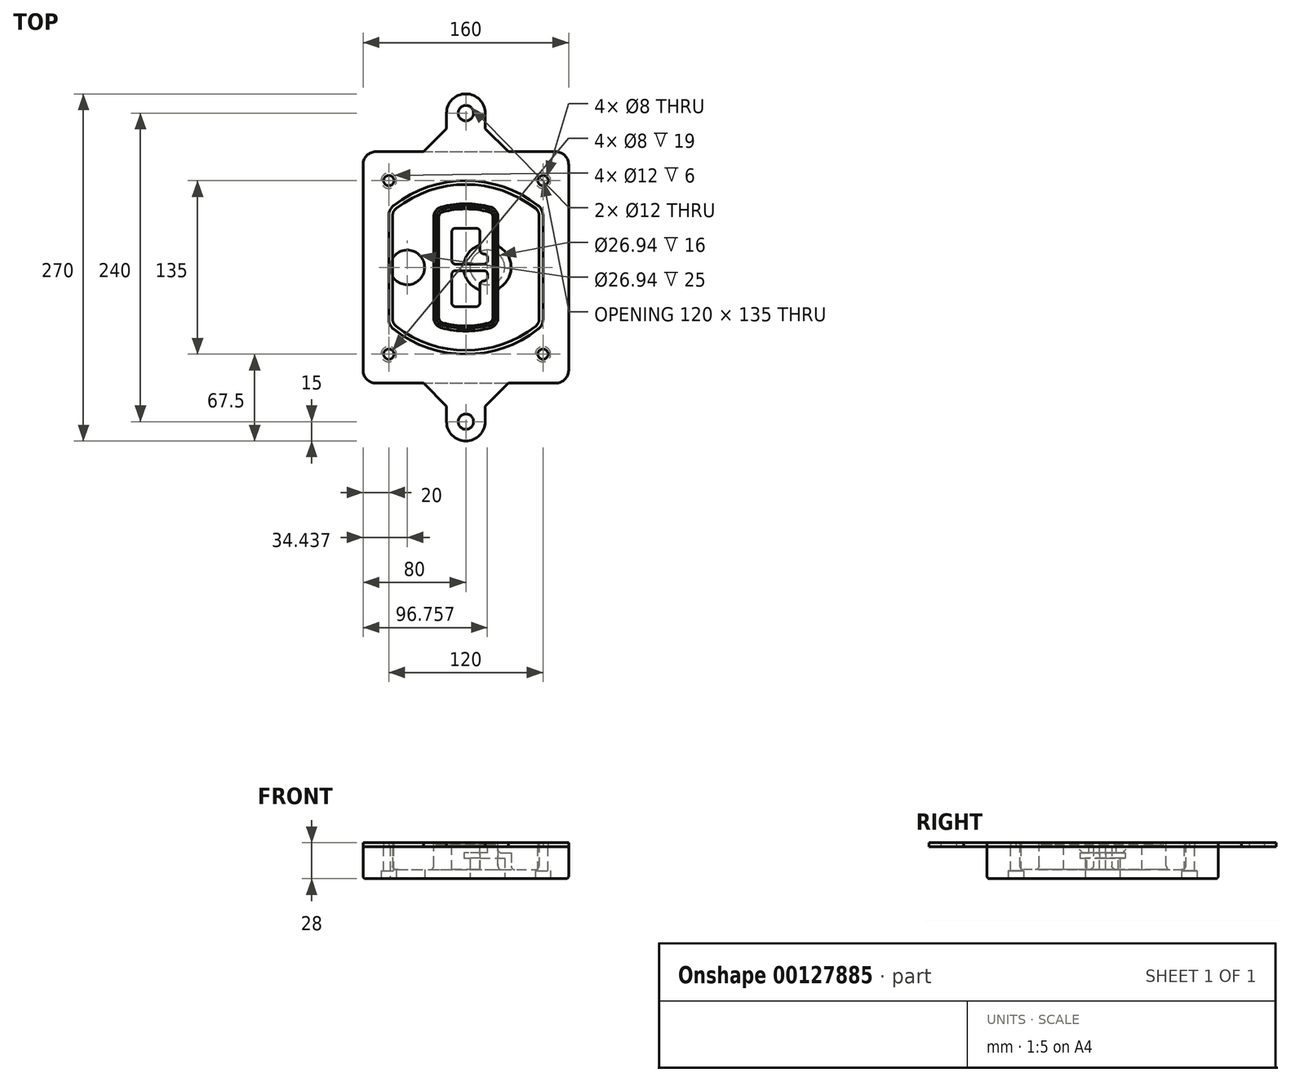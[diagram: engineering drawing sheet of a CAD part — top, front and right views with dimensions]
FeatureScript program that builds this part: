
annotation { "Feature Type Name" : "Feature", "Feature Type Description" : "" }
export const myFeature = defineFeature(function(context is Context, id is Id, definition is map)
    precondition{}
    {
        {
            var Q0;
            Q0=qCreatedBy(makeId("Top.planeOp"),FACE);
            var sketch = newSketch(context, id + "F0", { "sketchPlane" : qUnion([Q0])});
            skPoint(sketch, "E0.rect.middle", {"position": v(0, 0) * mm});
            skLineSegment(sketch, "E1.bottom", {"start": v(-70, -90) * mm, "end": v(70, -90) * mm});
            skLineSegment(sketch, "E1.top", {"start": v(-70, 90) * mm, "end": v(70, 90) * mm});
            skLineSegment(sketch, "E1.left", {"start": v(-80, -80) * mm, "end": v(-80, 80) * mm});
            skLineSegment(sketch, "E1.right", {"start": v(80, -80) * mm, "end": v(80, 80) * mm});
            skLineSegment(sketch, "E2", {"start": v(-80, 90) * mm, "end": v(80, -90) * mm, "construction": true});
            skLineSegment(sketch, "E3", {"start": v(80, 90) * mm, "end": v(-80, -90) * mm, "construction": true});
            skCircle(sketch, "E4", {"center": v(-60, 67.5) * mm, "radius": 4 * mm});
            skCircle(sketch, "E5", {"center": v(60, 67.5) * mm, "radius": 4 * mm});
            skCircle(sketch, "E6", {"center": v(60, -67.5) * mm, "radius": 4 * mm});
            skCircle(sketch, "E7", {"center": v(-60, -67.5) * mm, "radius": 4 * mm});
            skLineSegment(sketch, "E8", {"start": v(-60, 67.5) * mm, "end": v(60, 67.5) * mm, "construction": true});
            skLineSegment(sketch, "E9", {"start": v(60, 67.5) * mm, "end": v(60, -67.5) * mm, "construction": true});
            skLineSegment(sketch, "E10", {"start": v(60, -67.5) * mm, "end": v(-60, -67.5) * mm, "construction": true});
            skLineSegment(sketch, "E11", {"start": v(-60, -67.5) * mm, "end": v(-60, 67.5) * mm, "construction": true});
            skLineSegment(sketch, "E12", {"start": v(-60, 40.3) * mm, "end": v(-60, -40.3) * mm});
            skLineSegment(sketch, "E13", {"start": v(60, 40.3) * mm, "end": v(60, -40.3) * mm});
            skArc(sketch, "E14", {"start": v(56.15, 48.18) * mm, "mid": v(0, 67.5) * mm, "end": v(-56.15, 48.18) * mm});
            skArc(sketch, "E15", {"start": v(-56.15, -48.18) * mm, "mid": v(0, -67.5) * mm, "end": v(56.15, -48.18) * mm});
            skLineSegment(sketch, "E16", {"start": v(-60, 0) * mm, "end": v(60, 0) * mm, "construction": true});
            skPoint(sketch, "E17.visualSharp", {"position": v(-60, -45) * mm});
            skArc(sketch, "E17.filletArc", {"start": v(-60, -40.3) * mm, "mid": v(-58.99, -44.68) * mm, "end": v(-56.15, -48.18) * mm});
            skPoint(sketch, "E18.visualSharp", {"position": v(-60, 45) * mm});
            skArc(sketch, "E18.filletArc", {"start": v(-56.15, 48.18) * mm, "mid": v(-58.99, 44.68) * mm, "end": v(-60, 40.3) * mm});
            skPoint(sketch, "E19.visualSharp", {"position": v(60, 45) * mm});
            skArc(sketch, "E19.filletArc", {"start": v(60, 40.3) * mm, "mid": v(58.99, 44.68) * mm, "end": v(56.15, 48.18) * mm});
            skPoint(sketch, "E20.visualSharp", {"position": v(60, -45) * mm});
            skArc(sketch, "E20.filletArc", {"start": v(56.15, -48.18) * mm, "mid": v(58.99, -44.68) * mm, "end": v(60, -40.3) * mm});
            skPoint(sketch, "E21.visualSharp", {"position": v(-80, 90) * mm});
            skArc(sketch, "E21.filletArc", {"start": v(-70, 90) * mm, "mid": v(-77.07, 87.07) * mm, "end": v(-80, 80) * mm});
            skPoint(sketch, "E22.visualSharp", {"position": v(80, 90) * mm});
            skArc(sketch, "E22.filletArc", {"start": v(80, 80) * mm, "mid": v(77.07, 87.07) * mm, "end": v(70, 90) * mm});
            skPoint(sketch, "E23.visualSharp", {"position": v(80, -90) * mm});
            skArc(sketch, "E23.filletArc", {"start": v(70, -90) * mm, "mid": v(77.07, -87.07) * mm, "end": v(80, -80) * mm});
            skPoint(sketch, "E24.visualSharp", {"position": v(-80, -90) * mm});
            skArc(sketch, "E24.filletArc", {"start": v(-80, -80) * mm, "mid": v(-77.07, -87.07) * mm, "end": v(-70, -90) * mm});
            skArc(sketch, "E25.0", {"start": v(57, 40.3) * mm, "mid": v(56.3, 43.36) * mm, "end": v(54.3, 45.81) * mm});
            skLineSegment(sketch, "E25.1", {"start": v(57, 40.3) * mm, "end": v(57, -40.3) * mm});
            skArc(sketch, "E25.2", {"start": v(54.3, -45.81) * mm, "mid": v(56.3, -43.36) * mm, "end": v(57, -40.3) * mm});
            skArc(sketch, "E25.3", {"start": v(-54.3, -45.81) * mm, "mid": v(0, -64.5) * mm, "end": v(54.3, -45.81) * mm});
            skArc(sketch, "E25.4", {"start": v(-57, -40.3) * mm, "mid": v(-56.3, -43.36) * mm, "end": v(-54.3, -45.81) * mm});
            skArc(sketch, "E25.5", {"start": v(54.3, 45.81) * mm, "mid": v(0, 64.5) * mm, "end": v(-54.3, 45.81) * mm});
            skLineSegment(sketch, "E25.6", {"start": v(-57, 40.3) * mm, "end": v(-57, -40.3) * mm});
            skArc(sketch, "E25.7", {"start": v(-54.3, 45.81) * mm, "mid": v(-56.3, 43.36) * mm, "end": v(-57, 40.3) * mm});
            skArc(sketch, "E26.0", {"start": v(-58.62, 51.33) * mm, "mid": v(-62.58, 46.43) * mm, "end": v(-64, 40.3) * mm});
            skArc(sketch, "E26.1", {"start": v(58.62, 51.33) * mm, "mid": v(0, 71.5) * mm, "end": v(-58.62, 51.33) * mm});
            skArc(sketch, "E26.2", {"start": v(64, 40.3) * mm, "mid": v(62.58, 46.43) * mm, "end": v(58.62, 51.33) * mm});
            skLineSegment(sketch, "E26.3", {"start": v(64, 40.3) * mm, "end": v(64, -40.3) * mm});
            skArc(sketch, "E26.4", {"start": v(58.62, -51.33) * mm, "mid": v(62.58, -46.43) * mm, "end": v(64, -40.3) * mm});
            skLineSegment(sketch, "E26.5", {"start": v(-64, 40.3) * mm, "end": v(-64, -40.3) * mm});
            skArc(sketch, "E26.6", {"start": v(-58.62, -51.33) * mm, "mid": v(0, -71.5) * mm, "end": v(58.62, -51.33) * mm});
            skArc(sketch, "E26.7", {"start": v(-64, -40.3) * mm, "mid": v(-62.58, -46.43) * mm, "end": v(-58.62, -51.33) * mm});
            skSolve(sketch);
        }
        {
            var Q0;
            Q0=makeQuery(id+"F0.imprint","IMPRINT",FACE,{"disambiguationData":[TD([[makeQuery(id+"F0.imprint","IMPRINT",EDGE,{"derivedFrom":sQuery(id+"F0.wireOp",EDGE,"E1.bottom")}),1.0]])]});
            var Q1;
            Q1=makeQuery(id+"F0.imprint","IMPRINT",FACE,{"disambiguationData":[TD([[makeQuery(id+"F0.imprint","IMPRINT",EDGE,{"derivedFrom":sQuery(id+"F0.wireOp",EDGE,"E12")}),1.0]])]});
            var Q2;
            Q2=makeQuery(id+"F0.imprint","IMPRINT",FACE,{"disambiguationData":[TD([[makeQuery(id+"F0.imprint","IMPRINT",EDGE,{"derivedFrom":sQuery(id+"F0.wireOp",EDGE,"E25.0")}),1.0]])]});
            var Q3;
            Q3=makeQuery(id+"F0.imprint","IMPRINT",FACE,{"disambiguationData":[TD([[makeQuery(id+"F0.imprint","IMPRINT",EDGE,{"derivedFrom":sQuery(id+"F0.wireOp",EDGE,"E12")}),-1.0]])]});
            extrude(context, id + "F1", {"entities" : qUnion([Q0, Q1, Q2, Q3]), "oppositeDirection" : true, "depth" : 25 * mm});
        }
        {
            var Q0;
            Q0=makeQuery(id+"F0.imprint","IMPRINT",FACE,{"disambiguationData":[TD([[makeQuery(id+"F0.imprint","IMPRINT",EDGE,{"derivedFrom":sQuery(id+"F0.wireOp",EDGE,"E12")}),1.0]])]});
            extrude(context, id + "F2", {"entities" : qUnion([Q0]), "operationType" : NewBodyOperationType.ADD, "depth" : 3 * mm});
        }
        {
            var Q0;
            Q0=makeQuery(id+"F0.imprint","IMPRINT",FACE,{"disambiguationData":[TD([[makeQuery(id+"F0.imprint","IMPRINT",EDGE,{"derivedFrom":sQuery(id+"F0.wireOp",EDGE,"E25.0")}),1.0]])]});
            extrude(context, id + "F3", {"entities" : qUnion([Q0]), "operationType" : NewBodyOperationType.REMOVE, "oppositeDirection" : true, "depth" : 18 * mm});
        }
        {
            var Q0;
            Q0=makeQuery(id+"F2.opExtrude","CAP_FACE",FACE,{"disambiguationData":[OSD([sQuery(id+"F0.wireOp",EDGE,"E12"),sQuery(id+"F0.wireOp",EDGE,"E13"),sQuery(id+"F0.wireOp",EDGE,"E14"),sQuery(id+"F0.wireOp",EDGE,"E15"),sQuery(id+"F0.wireOp",EDGE,"E17.filletArc"),sQuery(id+"F0.wireOp",EDGE,"E18.filletArc"),sQuery(id+"F0.wireOp",EDGE,"E19.filletArc"),sQuery(id+"F0.wireOp",EDGE,"E20.filletArc"),sQuery(id+"F0.wireOp",EDGE,"E25.0"),sQuery(id+"F0.wireOp",EDGE,"E25.1"),sQuery(id+"F0.wireOp",EDGE,"E25.2"),sQuery(id+"F0.wireOp",EDGE,"E25.3"),sQuery(id+"F0.wireOp",EDGE,"E25.4"),sQuery(id+"F0.wireOp",EDGE,"E25.5"),sQuery(id+"F0.wireOp",EDGE,"E25.6"),sQuery(id+"F0.wireOp",EDGE,"E25.7")])],"isStart":false});
            var sketch = newSketch(context, id + "F4", { "sketchPlane" : qUnion([Q0])});
            skArc(sketch, "E27.0", {"start": v(-19.08, -46.97) * mm, "mid": v(0, -49.5) * mm, "end": v(19.08, -46.97) * mm});
            skArc(sketch, "E28.0", {"start": v(19.08, 46.97) * mm, "mid": v(0, 49.5) * mm, "end": v(-19.08, 46.97) * mm});
            skLineSegment(sketch, "E29", {"start": v(-25, 39.25) * mm, "end": v(-25, -39.25) * mm});
            skLineSegment(sketch, "E30", {"start": v(25, 39.25) * mm, "end": v(25, -39.25) * mm});
            skLineSegment(sketch, "E31", {"start": v(-25, 45.1) * mm, "end": v(25, 45.1) * mm, "construction": true});
            skLineSegment(sketch, "E32", {"start": v(-25, -45.1) * mm, "end": v(25, -45.1) * mm, "construction": true});
            skPoint(sketch, "E33.visualSharp", {"position": v(-25, 45.1) * mm});
            skArc(sketch, "E33.filletArc", {"start": v(-19.08, 46.97) * mm, "mid": v(-23.35, 44.11) * mm, "end": v(-25, 39.25) * mm});
            skPoint(sketch, "E34.visualSharp", {"position": v(25, 45.1) * mm});
            skArc(sketch, "E34.filletArc", {"start": v(25, 39.25) * mm, "mid": v(23.35, 44.11) * mm, "end": v(19.08, 46.97) * mm});
            skPoint(sketch, "E35.visualSharp", {"position": v(25, -45.1) * mm});
            skArc(sketch, "E35.filletArc", {"start": v(19.08, -46.97) * mm, "mid": v(23.35, -44.11) * mm, "end": v(25, -39.25) * mm});
            skPoint(sketch, "E36.visualSharp", {"position": v(-25, -45.1) * mm});
            skArc(sketch, "E36.filletArc", {"start": v(-25, -39.25) * mm, "mid": v(-23.35, -44.11) * mm, "end": v(-19.08, -46.97) * mm});
            skArc(sketch, "E37.0", {"start": v(54.3, 45.81) * mm, "mid": v(0, 64.5) * mm, "end": v(-54.3, 45.81) * mm});
            skArc(sketch, "E37.1", {"start": v(-54.3, 45.81) * mm, "mid": v(-56.3, 43.36) * mm, "end": v(-57, 40.3) * mm});
            skLineSegment(sketch, "E37.2", {"start": v(-57, 40.3) * mm, "end": v(-57, -40.3) * mm});
            skArc(sketch, "E37.3", {"start": v(-57, -40.3) * mm, "mid": v(-56.3, -43.36) * mm, "end": v(-54.3, -45.81) * mm});
            skArc(sketch, "E37.4", {"start": v(-54.3, -45.81) * mm, "mid": v(0, -64.5) * mm, "end": v(54.3, -45.81) * mm});
            skArc(sketch, "E37.5", {"start": v(54.3, -45.81) * mm, "mid": v(56.3, -43.36) * mm, "end": v(57, -40.3) * mm});
            skLineSegment(sketch, "E37.6", {"start": v(57, 40.3) * mm, "end": v(57, -40.3) * mm});
            skArc(sketch, "E37.7", {"start": v(57, 40.3) * mm, "mid": v(56.3, 43.36) * mm, "end": v(54.3, 45.81) * mm});
            skLineSegment(sketch, "E38.0", {"start": v(23, 39.25) * mm, "end": v(23, -39.25) * mm});
            skArc(sketch, "E38.1", {"start": v(18.56, -45.04) * mm, "mid": v(21.76, -42.9) * mm, "end": v(23, -39.25) * mm});
            skArc(sketch, "E38.2", {"start": v(-18.56, -45.04) * mm, "mid": v(0, -47.5) * mm, "end": v(18.56, -45.04) * mm});
            skArc(sketch, "E38.3", {"start": v(-23, -39.25) * mm, "mid": v(-21.76, -42.9) * mm, "end": v(-18.56, -45.04) * mm});
            skLineSegment(sketch, "E38.4", {"start": v(-23, 39.25) * mm, "end": v(-23, -39.25) * mm});
            skArc(sketch, "E38.5", {"start": v(23, 39.25) * mm, "mid": v(21.76, 42.9) * mm, "end": v(18.56, 45.04) * mm});
            skArc(sketch, "E38.6", {"start": v(-18.56, 45.04) * mm, "mid": v(-21.76, 42.9) * mm, "end": v(-23, 39.25) * mm});
            skArc(sketch, "E38.7", {"start": v(18.56, 45.04) * mm, "mid": v(0, 47.5) * mm, "end": v(-18.56, 45.04) * mm});
            skArc(sketch, "E39.0", {"start": v(21, 39.25) * mm, "mid": v(20.18, 41.68) * mm, "end": v(18.04, 43.1) * mm});
            skLineSegment(sketch, "E39.1", {"start": v(21, 39.25) * mm, "end": v(21, -39.25) * mm});
            skArc(sketch, "E39.2", {"start": v(18.04, -43.1) * mm, "mid": v(20.18, -41.68) * mm, "end": v(21, -39.25) * mm});
            skArc(sketch, "E39.3", {"start": v(-18.04, -43.1) * mm, "mid": v(0, -45.5) * mm, "end": v(18.04, -43.1) * mm});
            skArc(sketch, "E39.4", {"start": v(-21, -39.25) * mm, "mid": v(-20.18, -41.68) * mm, "end": v(-18.04, -43.1) * mm});
            skArc(sketch, "E39.5", {"start": v(18.04, 43.1) * mm, "mid": v(0, 45.5) * mm, "end": v(-18.04, 43.1) * mm});
            skLineSegment(sketch, "E39.6", {"start": v(-21, 39.25) * mm, "end": v(-21, -39.25) * mm});
            skArc(sketch, "E39.7", {"start": v(-18.04, 43.1) * mm, "mid": v(-20.18, 41.68) * mm, "end": v(-21, 39.25) * mm});
            skLineSegment(sketch, "E40", {"start": v(-25, 0) * mm, "end": v(25, 0) * mm, "construction": true});
            skLineSegment(sketch, "E41", {"start": v(-11, 5.5) * mm, "end": v(-11, 27.5) * mm});
            skLineSegment(sketch, "E42", {"start": v(-8, 30.5) * mm, "end": v(8, 30.5) * mm});
            skLineSegment(sketch, "E43", {"start": v(11, 27.5) * mm, "end": v(11, 13.5) * mm});
            skLineSegment(sketch, "E44", {"start": v(14, 10.5) * mm, "end": v(14, 10.5) * mm});
            skLineSegment(sketch, "E45", {"start": v(17, 7.5) * mm, "end": v(17, 5.5) * mm});
            skLineSegment(sketch, "E46", {"start": v(14, 2.5) * mm, "end": v(-8, 2.5) * mm});
            skPoint(sketch, "E47.visualSharp", {"position": v(-11, 30.5) * mm});
            skArc(sketch, "E47.filletArc", {"start": v(-8, 30.5) * mm, "mid": v(-10.12, 29.62) * mm, "end": v(-11, 27.5) * mm});
            skPoint(sketch, "E48.visualSharp", {"position": v(11, 30.5) * mm});
            skArc(sketch, "E48.filletArc", {"start": v(11, 27.5) * mm, "mid": v(10.12, 29.62) * mm, "end": v(8, 30.5) * mm});
            skPoint(sketch, "E49.visualSharp", {"position": v(11, 10.5) * mm});
            skArc(sketch, "E49.filletArc", {"start": v(11, 13.5) * mm, "mid": v(11.88, 11.38) * mm, "end": v(14, 10.5) * mm});
            skPoint(sketch, "E50.visualSharp", {"position": v(17, 10.5) * mm});
            skArc(sketch, "E50.filletArc", {"start": v(17, 7.5) * mm, "mid": v(16.12, 9.62) * mm, "end": v(14, 10.5) * mm});
            skPoint(sketch, "E51.visualSharp", {"position": v(17, 2.5) * mm});
            skArc(sketch, "E51.filletArc", {"start": v(14, 2.5) * mm, "mid": v(16.12, 3.38) * mm, "end": v(17, 5.5) * mm});
            skPoint(sketch, "E52.visualSharp", {"position": v(-11, 2.5) * mm});
            skArc(sketch, "E52.filletArc", {"start": v(-11, 5.5) * mm, "mid": v(-10.12, 3.38) * mm, "end": v(-8, 2.5) * mm});
            skLineSegment(sketch, "E53.0.MirrorCS", {"start": v(14, -2.5) * mm, "end": v(-8, -2.5) * mm});
            skArc(sketch, "E54.0.MirrorCS", {"start": v(-11, -5.5) * mm, "mid": v(-10.12, -3.38) * mm, "end": v(-8, -2.5) * mm});
            skLineSegment(sketch, "E55.0.MirrorCS", {"start": v(-11, -5.5) * mm, "end": v(-11, -27.5) * mm});
            skArc(sketch, "E56.0.MirrorCS", {"start": v(-8, -30.5) * mm, "mid": v(-10.12, -29.62) * mm, "end": v(-11, -27.5) * mm});
            skLineSegment(sketch, "E57.0.MirrorCS", {"start": v(-8, -30.5) * mm, "end": v(8, -30.5) * mm});
            skArc(sketch, "E58.0.MirrorCS", {"start": v(11, -27.5) * mm, "mid": v(10.12, -29.62) * mm, "end": v(8, -30.5) * mm});
            skLineSegment(sketch, "E59.0.MirrorCS", {"start": v(11, -27.5) * mm, "end": v(11, -13.5) * mm});
            skArc(sketch, "E60.0.MirrorCS", {"start": v(11, -13.5) * mm, "mid": v(11.88, -11.38) * mm, "end": v(14, -10.5) * mm});
            skArc(sketch, "E61.0.MirrorCS", {"start": v(17, -7.5) * mm, "mid": v(16.12, -9.62) * mm, "end": v(14, -10.5) * mm});
            skLineSegment(sketch, "E62.0.MirrorCS", {"start": v(17, -7.5) * mm, "end": v(17, -5.5) * mm});
            skArc(sketch, "E63.0.MirrorCS", {"start": v(14, -2.5) * mm, "mid": v(16.12, -3.38) * mm, "end": v(17, -5.5) * mm});
            skSolve(sketch);
        }
        {
            var Q0;
            Q0=makeQuery(id+"F4.imprint","IMPRINT",FACE,{"disambiguationData":[TD([[makeQuery(id+"F4.imprint","IMPRINT",EDGE,{"derivedFrom":sQuery(id+"F4.wireOp",EDGE,"E27.0")}),1.0]])]});
            var Q1;
            Q1=makeQuery(id+"F4.imprint","IMPRINT",FACE,{"disambiguationData":[TD([[makeQuery(id+"F4.imprint","IMPRINT",EDGE,{"derivedFrom":sQuery(id+"F4.wireOp",EDGE,"E38.0")}),-1.0]])]});
            var Q2;
            Q2=makeQuery(id+"F4.imprint","IMPRINT",FACE,{"disambiguationData":[TD([[makeQuery(id+"F4.imprint","IMPRINT",EDGE,{"derivedFrom":sQuery(id+"F4.wireOp",EDGE,"E39.0")}),1.0]])]});
            extrude(context, id + "F5", {"entities" : qUnion([Q0, Q1, Q2]), "operationType" : NewBodyOperationType.ADD, "endBound" : BoundingType.UP_TO_NEXT, "oppositeDirection" : true, "depth" : 25 * mm});
        }
        {
            var Q0;
            Q0=makeQuery(id+"F4.imprint","IMPRINT",FACE,{"disambiguationData":[TD([[makeQuery(id+"F4.imprint","IMPRINT",EDGE,{"derivedFrom":sQuery(id+"F4.wireOp",EDGE,"E38.0")}),-1.0]])]});
            extrude(context, id + "F6", {"entities" : qUnion([Q0]), "operationType" : NewBodyOperationType.REMOVE, "oppositeDirection" : true, "depth" : 2 * mm});
        }
        {
            var Q0;
            Q0=makeQuery(id+"F1.opExtrude","CAP_FACE",FACE,{"disambiguationData":[OSD([sQuery(id+"F0.wireOp",EDGE,"E1.bottom"),sQuery(id+"F0.wireOp",EDGE,"E1.top"),sQuery(id+"F0.wireOp",EDGE,"E1.left"),sQuery(id+"F0.wireOp",EDGE,"E1.right"),sQuery(id+"F0.wireOp",EDGE,"E4"),sQuery(id+"F0.wireOp",EDGE,"E5"),sQuery(id+"F0.wireOp",EDGE,"E6"),sQuery(id+"F0.wireOp",EDGE,"E7"),sQuery(id+"F0.wireOp",EDGE,"E21.filletArc"),sQuery(id+"F0.wireOp",EDGE,"E22.filletArc"),sQuery(id+"F0.wireOp",EDGE,"E23.filletArc"),sQuery(id+"F0.wireOp",EDGE,"E24.filletArc")])],"isStart":false});
            var sketch = newSketch(context, id + "F7", { "sketchPlane" : qUnion([Q0])});
            skCircle(sketch, "E64", {"center": v(16.76, 0) * mm, "radius": 13.47 * mm});
            skCircle(sketch, "E65", {"center": v(-45.56, 0) * mm, "radius": 13.47 * mm});
            skLineSegment(sketch, "E66", {"start": v(80, 0) * mm, "end": v(-80, 0) * mm});
            skCircle(sketch, "E67", {"center": v(16.76, 0) * mm, "radius": 18.47 * mm});
            skCircle(sketch, "E68", {"center": v(60, -67.5) * mm, "radius": 6 * mm});
            skCircle(sketch, "E69", {"center": v(-60, -67.5) * mm, "radius": 6 * mm});
            skCircle(sketch, "E70", {"center": v(-60, 67.5) * mm, "radius": 6 * mm});
            skCircle(sketch, "E71", {"center": v(60, 67.5) * mm, "radius": 6 * mm});
            skSolve(sketch);
        }
        {
            var Q0;
            {var subQ1=sQuery(id+"F7.wireOp",EDGE,"E66");var subQ4=sQuery(id+"F7.wireOp",EDGE,"E64");var subQ6=makeQuery(id+"F7.imprint","INTERSECT",VERTEX,{"disambiguationData":[OD(0.0)],"derivedFrom":[subQ4,subQ1]});Q0=makeQuery(id+"F7.imprint","IMPRINT",FACE,{"disambiguationData":[TD([[makeQuery(id+"F7.imprint","IMPRINT",EDGE,{"disambiguationData":[TD([[subQ6,-1.0]])],"derivedFrom":subQ4}),-1.0]])]});}
            var Q1;
            {var subQ0=sQuery(id+"F7.wireOp",EDGE,"E66");var subQ1=sQuery(id+"F7.wireOp",EDGE,"E64");var subQ3=makeQuery(id+"F7.imprint","INTERSECT",VERTEX,{"disambiguationData":[OD(0.0)],"derivedFrom":[subQ1,subQ0]});Q1=makeQuery(id+"F7.imprint","IMPRINT",FACE,{"disambiguationData":[TD([[makeQuery(id+"F7.imprint","IMPRINT",EDGE,{"disambiguationData":[TD([[subQ3,-1.0]])],"derivedFrom":subQ1}),1.0]])]});}
            var Q2;
            {var subQ0=sQuery(id+"F7.wireOp",EDGE,"E66");var subQ1=sQuery(id+"F7.wireOp",EDGE,"E64");var subQ3=makeQuery(id+"F7.imprint","INTERSECT",VERTEX,{"disambiguationData":[OD(0.0)],"derivedFrom":[subQ1,subQ0]});Q2=makeQuery(id+"F7.imprint","IMPRINT",FACE,{"disambiguationData":[TD([[makeQuery(id+"F7.imprint","IMPRINT",EDGE,{"disambiguationData":[TD([[subQ3,1.0]])],"derivedFrom":subQ1}),1.0]])]});}
            var Q3;
            {var subQ1=sQuery(id+"F7.wireOp",EDGE,"E66");var subQ4=sQuery(id+"F7.wireOp",EDGE,"E64");var subQ6=makeQuery(id+"F7.imprint","INTERSECT",VERTEX,{"disambiguationData":[OD(0.0)],"derivedFrom":[subQ4,subQ1]});Q3=makeQuery(id+"F7.imprint","IMPRINT",FACE,{"disambiguationData":[TD([[makeQuery(id+"F7.imprint","IMPRINT",EDGE,{"disambiguationData":[TD([[subQ6,1.0]])],"derivedFrom":subQ4}),-1.0]])]});}
            extrude(context, id + "F8", {"entities" : qUnion([Q0, Q1, Q2, Q3]), "operationType" : NewBodyOperationType.ADD, "oppositeDirection" : true, "depth" : 20 * mm});
        }
        {
            var Q0;
            {var subQ0=sQuery(id+"F7.wireOp",EDGE,"E66");var subQ1=sQuery(id+"F7.wireOp",EDGE,"E64");var subQ3=makeQuery(id+"F7.imprint","INTERSECT",VERTEX,{"disambiguationData":[OD(0.0)],"derivedFrom":[subQ1,subQ0]});Q0=makeQuery(id+"F7.imprint","IMPRINT",FACE,{"disambiguationData":[TD([[makeQuery(id+"F7.imprint","IMPRINT",EDGE,{"disambiguationData":[TD([[subQ3,-1.0]])],"derivedFrom":subQ1}),1.0]])]});}
            var Q1;
            {var subQ0=sQuery(id+"F7.wireOp",EDGE,"E66");var subQ1=sQuery(id+"F7.wireOp",EDGE,"E64");var subQ3=makeQuery(id+"F7.imprint","INTERSECT",VERTEX,{"disambiguationData":[OD(0.0)],"derivedFrom":[subQ1,subQ0]});Q1=makeQuery(id+"F7.imprint","IMPRINT",FACE,{"disambiguationData":[TD([[makeQuery(id+"F7.imprint","IMPRINT",EDGE,{"disambiguationData":[TD([[subQ3,1.0]])],"derivedFrom":subQ1}),1.0]])]});}
            extrude(context, id + "F9", {"entities" : qUnion([Q0, Q1]), "operationType" : NewBodyOperationType.REMOVE, "oppositeDirection" : true, "depth" : 16 * mm});
        }
        {
            var Q0;
            {var subQ0=sQuery(id+"F7.wireOp",EDGE,"E66");var subQ1=sQuery(id+"F7.wireOp",EDGE,"E65");var subQ3=makeQuery(id+"F7.imprint","INTERSECT",VERTEX,{"disambiguationData":[OD(0.0)],"derivedFrom":[subQ1,subQ0]});Q0=makeQuery(id+"F7.imprint","IMPRINT",FACE,{"disambiguationData":[TD([[makeQuery(id+"F7.imprint","IMPRINT",EDGE,{"disambiguationData":[TD([[subQ3,-1.0]])],"derivedFrom":subQ1}),1.0]])]});}
            var Q1;
            {var subQ0=sQuery(id+"F7.wireOp",EDGE,"E66");var subQ1=sQuery(id+"F7.wireOp",EDGE,"E65");var subQ3=makeQuery(id+"F7.imprint","INTERSECT",VERTEX,{"disambiguationData":[OD(0.0)],"derivedFrom":[subQ1,subQ0]});Q1=makeQuery(id+"F7.imprint","IMPRINT",FACE,{"disambiguationData":[TD([[makeQuery(id+"F7.imprint","IMPRINT",EDGE,{"disambiguationData":[TD([[subQ3,1.0]])],"derivedFrom":subQ1}),1.0]])]});}
            extrude(context, id + "F10", {"entities" : qUnion([Q0, Q1]), "operationType" : NewBodyOperationType.REMOVE, "oppositeDirection" : true, "depth" : 25 * mm});
        }
        {
            var Q0;
            Q0=makeQuery(id+"F7.imprint","IMPRINT",FACE,{"disambiguationData":[TD([[makeQuery(id+"F7.imprint","IMPRINT",EDGE,{"derivedFrom":sQuery(id+"F7.wireOp",EDGE,"E68")}),1.0]])]});
            var Q1;
            Q1=makeQuery(id+"F7.imprint","IMPRINT",FACE,{"disambiguationData":[TD([[makeQuery(id+"F7.imprint","IMPRINT",EDGE,{"derivedFrom":makeQuery(id+"F1.opExtrude","CAP_EDGE",EDGE,{"disambiguationData":[OSD([sQuery(id+"F0.wireOp",EDGE,"E5")])],"isStart":false})}),-1.0]])]});
            var Q2;
            Q2=makeQuery(id+"F7.imprint","IMPRINT",FACE,{"disambiguationData":[TD([[makeQuery(id+"F7.imprint","IMPRINT",EDGE,{"derivedFrom":sQuery(id+"F7.wireOp",EDGE,"E69")}),1.0]])]});
            var Q3;
            Q3=makeQuery(id+"F7.imprint","IMPRINT",FACE,{"disambiguationData":[TD([[makeQuery(id+"F7.imprint","IMPRINT",EDGE,{"derivedFrom":makeQuery(id+"F1.opExtrude","CAP_EDGE",EDGE,{"disambiguationData":[OSD([sQuery(id+"F0.wireOp",EDGE,"E4")])],"isStart":false})}),-1.0]])]});
            var Q4;
            Q4=makeQuery(id+"F7.imprint","IMPRINT",FACE,{"disambiguationData":[TD([[makeQuery(id+"F7.imprint","IMPRINT",EDGE,{"derivedFrom":sQuery(id+"F7.wireOp",EDGE,"E70")}),1.0]])]});
            var Q5;
            Q5=makeQuery(id+"F7.imprint","IMPRINT",FACE,{"disambiguationData":[TD([[makeQuery(id+"F7.imprint","IMPRINT",EDGE,{"derivedFrom":makeQuery(id+"F1.opExtrude","CAP_EDGE",EDGE,{"disambiguationData":[OSD([sQuery(id+"F0.wireOp",EDGE,"E7")])],"isStart":false})}),-1.0]])]});
            var Q6;
            Q6=makeQuery(id+"F7.imprint","IMPRINT",FACE,{"disambiguationData":[TD([[makeQuery(id+"F7.imprint","IMPRINT",EDGE,{"derivedFrom":sQuery(id+"F7.wireOp",EDGE,"E71")}),1.0]])]});
            var Q7;
            Q7=makeQuery(id+"F7.imprint","IMPRINT",FACE,{"disambiguationData":[TD([[makeQuery(id+"F7.imprint","IMPRINT",EDGE,{"derivedFrom":makeQuery(id+"F1.opExtrude","CAP_EDGE",EDGE,{"disambiguationData":[OSD([sQuery(id+"F0.wireOp",EDGE,"E6")])],"isStart":false})}),-1.0]])]});
            extrude(context, id + "F11", {"entities" : qUnion([Q0, Q1, Q2, Q3, Q4, Q5, Q6, Q7]), "operationType" : NewBodyOperationType.REMOVE, "oppositeDirection" : true, "depth" : 6 * mm});
        }
        {
            var Q0;
            Q0=makeQuery(id+"F9.boolean.opBoolean","COPY",FACE,{"derivedFrom":makeQuery(id+"F9.opExtrude","CAP_FACE",FACE,{"disambiguationData":[OSD([sQuery(id+"F7.wireOp",EDGE,"E64")])],"isStart":false})});
            var sketch = newSketch(context, id + "F12", { "sketchPlane" : qUnion([Q0])});
            skArc(sketch, "E72.0", {"start": v(11, 17.55) * mm, "mid": v(2.57, 11.82) * mm, "end": v(-1.54, 2.5) * mm});
            skArc(sketch, "E72.1", {"start": v(-1.54, -2.5) * mm, "mid": v(2.57, -11.82) * mm, "end": v(11, -17.55) * mm});
            skLineSegment(sketch, "E73", {"start": v(-1.54, -2.5) * mm, "end": v(14, -2.5) * mm});
            skLineSegment(sketch, "E74.0", {"start": v(14, 2.5) * mm, "end": v(-1.54, 2.5) * mm});
            skArc(sketch, "E74.1", {"start": v(14, 2.5) * mm, "mid": v(16.12, 3.38) * mm, "end": v(17, 5.5) * mm});
            skLineSegment(sketch, "E74.2", {"start": v(17, 7.5) * mm, "end": v(17, 5.5) * mm});
            skArc(sketch, "E74.3", {"start": v(17, 7.5) * mm, "mid": v(16.12, 9.62) * mm, "end": v(14, 10.5) * mm});
            skArc(sketch, "E74.4", {"start": v(11, 13.5) * mm, "mid": v(11.88, 11.38) * mm, "end": v(14, 10.5) * mm});
            skLineSegment(sketch, "E74.5", {"start": v(11, 17.55) * mm, "end": v(11, 13.5) * mm});
            skLineSegment(sketch, "E74.7", {"start": v(14, -2.5) * mm, "end": v(-1.54, -2.5) * mm});
            skArc(sketch, "E74.8", {"start": v(14, -2.5) * mm, "mid": v(16.12, -3.38) * mm, "end": v(17, -5.5) * mm});
            skLineSegment(sketch, "E74.9", {"start": v(17, -7.5) * mm, "end": v(17, -5.5) * mm});
            skArc(sketch, "E74.10", {"start": v(17, -7.5) * mm, "mid": v(16.12, -9.62) * mm, "end": v(14, -10.5) * mm});
            skArc(sketch, "E74.11", {"start": v(11, -13.5) * mm, "mid": v(11.88, -11.38) * mm, "end": v(14, -10.5) * mm});
            skLineSegment(sketch, "E74.12", {"start": v(11, -17.55) * mm, "end": v(11, -13.5) * mm});
            skPoint(sketch, "E75.orphan", {"position": v(11, -27.5) * mm});
            skPoint(sketch, "E76.orphan", {"position": v(-8, -2.5) * mm});
            skPoint(sketch, "E77.orphan", {"position": v(-8, 2.5) * mm});
            skPoint(sketch, "E78.orphan", {"position": v(11, 27.5) * mm});
            skSolve(sketch);
        }
        {
            var Q0;
            {var subQ7=sQuery(id+"F12.wireOp",EDGE,"E72.0");var subQ14=sQuery(id+"F12.wireOp",EDGE,"E72.1");var subQ16=sQuery(id+"F12.wireOp",EDGE,"E74.1");var subQ18=sQuery(id+"F12.wireOp",EDGE,"E74.8");Q0=qUnion([makeQuery(id+"F12.imprint","IMPRINT",FACE,{"disambiguationData":[TD([[makeQuery(id+"F12.imprint","IMPRINT",EDGE,{"derivedFrom":subQ7}),1.0]])]}),makeQuery(id+"F12.imprint","IMPRINT",FACE,{"disambiguationData":[TD([[makeQuery(id+"F12.imprint","IMPRINT",EDGE,{"derivedFrom":subQ14}),1.0]])]}),makeQuery(id+"F12.imprint","IMPRINT",FACE,{"disambiguationData":[TD([[makeQuery(id+"F12.imprint","IMPRINT",EDGE,{"derivedFrom":subQ16}),1.0]])]}),makeQuery(id+"F12.imprint","IMPRINT",FACE,{"disambiguationData":[TD([[makeQuery(id+"F12.imprint","IMPRINT",EDGE,{"derivedFrom":subQ18}),-1.0]])]})]);}
            var Q1;
            Q1=makeQuery(id+"F5.boolean.opBoolean","SPLIT",FACE,{"disambiguationData":[TD([makeQuery(id+"F5.opExtrude","SWEPT_FACE",FACE,{"disambiguationData":[OSD([sQuery(id+"F4.wireOp",EDGE,"E41")])]})])],"derivedFrom":makeQuery(id+"F3.boolean.opBoolean","COPY",FACE,{"derivedFrom":makeQuery(id+"F3.opExtrude","CAP_FACE",FACE,{"disambiguationData":[OSD([sQuery(id+"F0.wireOp",EDGE,"E25.0"),sQuery(id+"F0.wireOp",EDGE,"E25.1"),sQuery(id+"F0.wireOp",EDGE,"E25.2"),sQuery(id+"F0.wireOp",EDGE,"E25.3"),sQuery(id+"F0.wireOp",EDGE,"E25.4"),sQuery(id+"F0.wireOp",EDGE,"E25.5"),sQuery(id+"F0.wireOp",EDGE,"E25.6"),sQuery(id+"F0.wireOp",EDGE,"E25.7")])],"isStart":false})})});
            extrude(context, id + "F13", {"entities" : qUnion([Q0]), "operationType" : NewBodyOperationType.REMOVE, "endBound" : BoundingType.UP_TO_SURFACE, "endBoundEntityFace" : qUnion([Q1]), "depth" : 25 * mm});
        }
        {
            var Q0;
            Q0=makeQuery(id+"F3.boolean.opBoolean","COPY",EDGE,{"derivedFrom":makeQuery(id+"F3.opExtrude","CAP_EDGE",EDGE,{"disambiguationData":[OSD([sQuery(id+"F0.wireOp",EDGE,"E25.6")])],"isStart":false})});
            var Q1;
            Q1=makeQuery(id+"F8.boolean.opBoolean","INTERSECT",EDGE,{"derivedFrom":[makeQuery(id+"F5.opExtrude","SWEPT_FACE",FACE,{"disambiguationData":[OSD([sQuery(id+"F4.wireOp",EDGE,"E30")])]}),makeQuery(id+"F8.opExtrude","CAP_FACE",FACE,{"disambiguationData":[OSD([sQuery(id+"F7.wireOp",EDGE,"E67")])],"isStart":false})]});
            var Q2;
            Q2=makeQuery(id+"F8.boolean.opBoolean","INTERSECT",EDGE,{"disambiguationData":[OD(1.0)],"derivedFrom":[makeQuery(id+"F5.opExtrude","SWEPT_FACE",FACE,{"disambiguationData":[OSD([sQuery(id+"F4.wireOp",EDGE,"E30")])]}),makeQuery(id+"F8.opExtrude","SWEPT_FACE",FACE,{"disambiguationData":[OSD([sQuery(id+"F7.wireOp",EDGE,"E67")])]})]});
            var Q3;
            {var subQ0=sQuery(id+"F4.wireOp",EDGE,"E30");Q3=makeQuery(id+"F8.boolean.opBoolean","SPLIT",EDGE,{"disambiguationData":[TD([makeQuery(id+"F5.opExtrude","SWEPT_FACE",FACE,{"disambiguationData":[OSD([sQuery(id+"F4.wireOp",EDGE,"E35.filletArc")])]})])],"derivedFrom":makeQuery(id+"F5.opExtrude","CAP_EDGE",EDGE,{"disambiguationData":[OSD([subQ0])],"isStart":false})});}
            var Q4;
            {var subQ0=sQuery(id+"F0.wireOp",EDGE,"E25.7");var subQ1=sQuery(id+"F0.wireOp",EDGE,"E25.1");var subQ2=sQuery(id+"F0.wireOp",EDGE,"E25.6");var subQ3=sQuery(id+"F0.wireOp",EDGE,"E25.5");var subQ4=sQuery(id+"F0.wireOp",EDGE,"E25.4");var subQ5=sQuery(id+"F0.wireOp",EDGE,"E25.0");var subQ6=sQuery(id+"F0.wireOp",EDGE,"E25.2");var subQ7=sQuery(id+"F0.wireOp",EDGE,"E25.3");Q4=makeQuery(id+"F8.boolean.opBoolean","INTERSECT",EDGE,{"derivedFrom":[makeQuery(id+"F5.boolean.opBoolean","SPLIT",FACE,{"disambiguationData":[TD([makeQuery(id+"F2.opExtrude","SWEPT_FACE",FACE,{"disambiguationData":[OSD([subQ5])]})])],"derivedFrom":makeQuery(id+"F3.boolean.opBoolean","COPY",FACE,{"derivedFrom":makeQuery(id+"F3.opExtrude","CAP_FACE",FACE,{"disambiguationData":[OSD([subQ5,subQ1,subQ6,subQ7,subQ4,subQ3,subQ2,subQ0])],"isStart":false})})}),makeQuery(id+"F8.opExtrude","SWEPT_FACE",FACE,{"disambiguationData":[OSD([sQuery(id+"F7.wireOp",EDGE,"E67")])]})]});}
            var Q5;
            Q5=makeQuery(id+"F8.boolean.opBoolean","INTERSECT",EDGE,{"disambiguationData":[OD(0.0)],"derivedFrom":[makeQuery(id+"F5.opExtrude","SWEPT_FACE",FACE,{"disambiguationData":[OSD([sQuery(id+"F4.wireOp",EDGE,"E30")])]}),makeQuery(id+"F8.opExtrude","SWEPT_FACE",FACE,{"disambiguationData":[OSD([sQuery(id+"F7.wireOp",EDGE,"E67")])]})]});
            fillet(context, id + "F14", {"entities" : qUnion([Q0, Q1, Q2, Q3, Q4, Q5]), "radius" : 3 * mm, "tangentPropagation" : true, "allowEdgeOverflow" : false});
        }
        {
            var Q0;
            Q0=makeQuery(id+"F1.opExtrude","CAP_EDGE",EDGE,{"disambiguationData":[OSD([sQuery(id+"F0.wireOp",EDGE,"E1.bottom")])],"isStart":false});
            fillet(context, id + "F15", {"entities" : qUnion([Q0]), "radius" : 2 * mm, "tangentPropagation" : true, "allowEdgeOverflow" : false});
        }
        {
            var Q0;
            {var subQ0=sQuery(id+"F0.wireOp",EDGE,"E22.filletArc");var subQ1=sQuery(id+"F0.wireOp",EDGE,"E7");var subQ2=sQuery(id+"F0.wireOp",EDGE,"E6");var subQ3=sQuery(id+"F0.wireOp",EDGE,"E5");var subQ4=sQuery(id+"F0.wireOp",EDGE,"E4");var subQ5=sQuery(id+"F0.wireOp",EDGE,"E1.bottom");var subQ6=sQuery(id+"F0.wireOp",EDGE,"E21.filletArc");var subQ7=sQuery(id+"F0.wireOp",EDGE,"E1.top");var subQ8=sQuery(id+"F0.wireOp",EDGE,"E1.left");var subQ9=sQuery(id+"F0.wireOp",EDGE,"E1.right");var subQ10=sQuery(id+"F0.wireOp",EDGE,"E23.filletArc");var subQ11=sQuery(id+"F0.wireOp",EDGE,"E24.filletArc");Q0=makeQuery(id+"F2.boolean.opBoolean","SPLIT",FACE,{"disambiguationData":[TD([makeQuery(id+"F1.opExtrude","SWEPT_FACE",FACE,{"disambiguationData":[OSD([subQ5])]})])],"derivedFrom":makeQuery(id+"F1.opExtrude","CAP_FACE",FACE,{"disambiguationData":[OSD([subQ5,subQ7,subQ8,subQ9,subQ4,subQ3,subQ2,subQ1,subQ6,subQ0,subQ10,subQ11])],"isStart":true})});}
            var sketch = newSketch(context, id + "F16", { "sketchPlane" : qUnion([Q0])});
            skLineSegment(sketch, "E79", {"start": v(0, 90) * mm, "end": v(0, 120) * mm, "construction": true});
            skCircle(sketch, "E80", {"center": v(0, 120) * mm, "radius": 6 * mm});
            skLineSegment(sketch, "E81", {"start": v(-15, 120) * mm, "end": v(-15, 108) * mm});
            skLineSegment(sketch, "E82", {"start": v(-15, 108) * mm, "end": v(-33, 90) * mm});
            skLineSegment(sketch, "E83", {"start": v(15, 120) * mm, "end": v(15, 108) * mm});
            skLineSegment(sketch, "E84", {"start": v(15, 108) * mm, "end": v(33, 90) * mm});
            skArc(sketch, "E85", {"start": v(15, 120) * mm, "mid": v(0, 135) * mm, "end": v(-15, 120) * mm});
            skLineSegment(sketch, "E86", {"start": v(-33, 90) * mm, "end": v(33, 90) * mm});
            skLineSegment(sketch, "E87", {"start": v(-80, 0) * mm, "end": v(80, 0) * mm, "construction": true});
            skLineSegment(sketch, "E88.MirrorCS", {"start": v(-15, -108) * mm, "end": v(-33, -90) * mm});
            skLineSegment(sketch, "E89.MirrorCS", {"start": v(-15, -120) * mm, "end": v(-15, -108) * mm});
            skArc(sketch, "E90.MirrorCS", {"start": v(15, -120) * mm, "mid": v(0, -135) * mm, "end": v(-15, -120) * mm});
            skCircle(sketch, "E91.MirrorC", {"center": v(0, -120) * mm, "radius": 6 * mm});
            skLineSegment(sketch, "E92.MirrorCS", {"start": v(15, -120) * mm, "end": v(15, -108) * mm});
            skLineSegment(sketch, "E93.MirrorCS", {"start": v(15, -108) * mm, "end": v(33, -90) * mm});
            skLineSegment(sketch, "E94.MirrorCS", {"start": v(0, -90) * mm, "end": v(0, -120) * mm, "construction": true});
            skSolve(sketch);
        }
        {
            var Q0;
            {var subQ0=sQuery(id+"F16.wireOp",EDGE,"E88.MirrorCS");Q0=makeQuery(id+"F16.imprint","IMPRINT",FACE,{"disambiguationData":[TD([[makeQuery(id+"F16.imprint","IMPRINT",EDGE,{"derivedFrom":subQ0}),-1.0]])]});}
            var Q1;
            Q1=makeQuery(id+"F16.imprint","IMPRINT",FACE,{"disambiguationData":[TD([[makeQuery(id+"F16.imprint","IMPRINT",EDGE,{"derivedFrom":sQuery(id+"F16.wireOp",EDGE,"E80")}),-1.0]])]});
            var Q2;
            {var subQ5=sQuery(id+"F16.wireOp",EDGE,"E86");Q2=makeQuery(id+"F16.imprint","IMPRINT",FACE,{"disambiguationData":[TD([[makeQuery(id+"F16.imprint","IMPRINT",EDGE,{"derivedFrom":subQ5}),-1.0]])]});}
            var Q3;
            Q3=makeQuery(id+"F2.opExtrude","CAP_FACE",FACE,{"disambiguationData":[OSD([sQuery(id+"F0.wireOp",EDGE,"E12"),sQuery(id+"F0.wireOp",EDGE,"E13"),sQuery(id+"F0.wireOp",EDGE,"E14"),sQuery(id+"F0.wireOp",EDGE,"E15"),sQuery(id+"F0.wireOp",EDGE,"E17.filletArc"),sQuery(id+"F0.wireOp",EDGE,"E18.filletArc"),sQuery(id+"F0.wireOp",EDGE,"E19.filletArc"),sQuery(id+"F0.wireOp",EDGE,"E20.filletArc"),sQuery(id+"F0.wireOp",EDGE,"E25.0"),sQuery(id+"F0.wireOp",EDGE,"E25.1"),sQuery(id+"F0.wireOp",EDGE,"E25.2"),sQuery(id+"F0.wireOp",EDGE,"E25.3"),sQuery(id+"F0.wireOp",EDGE,"E25.4"),sQuery(id+"F0.wireOp",EDGE,"E25.5"),sQuery(id+"F0.wireOp",EDGE,"E25.6"),sQuery(id+"F0.wireOp",EDGE,"E25.7")])],"isStart":false});
            extrude(context, id + "F17", {"entities" : qUnion([Q0, Q1, Q2]), "endBound" : BoundingType.UP_TO_SURFACE, "endBoundEntityFace" : qUnion([Q3]), "depth" : 25 * mm});
        }
    });
